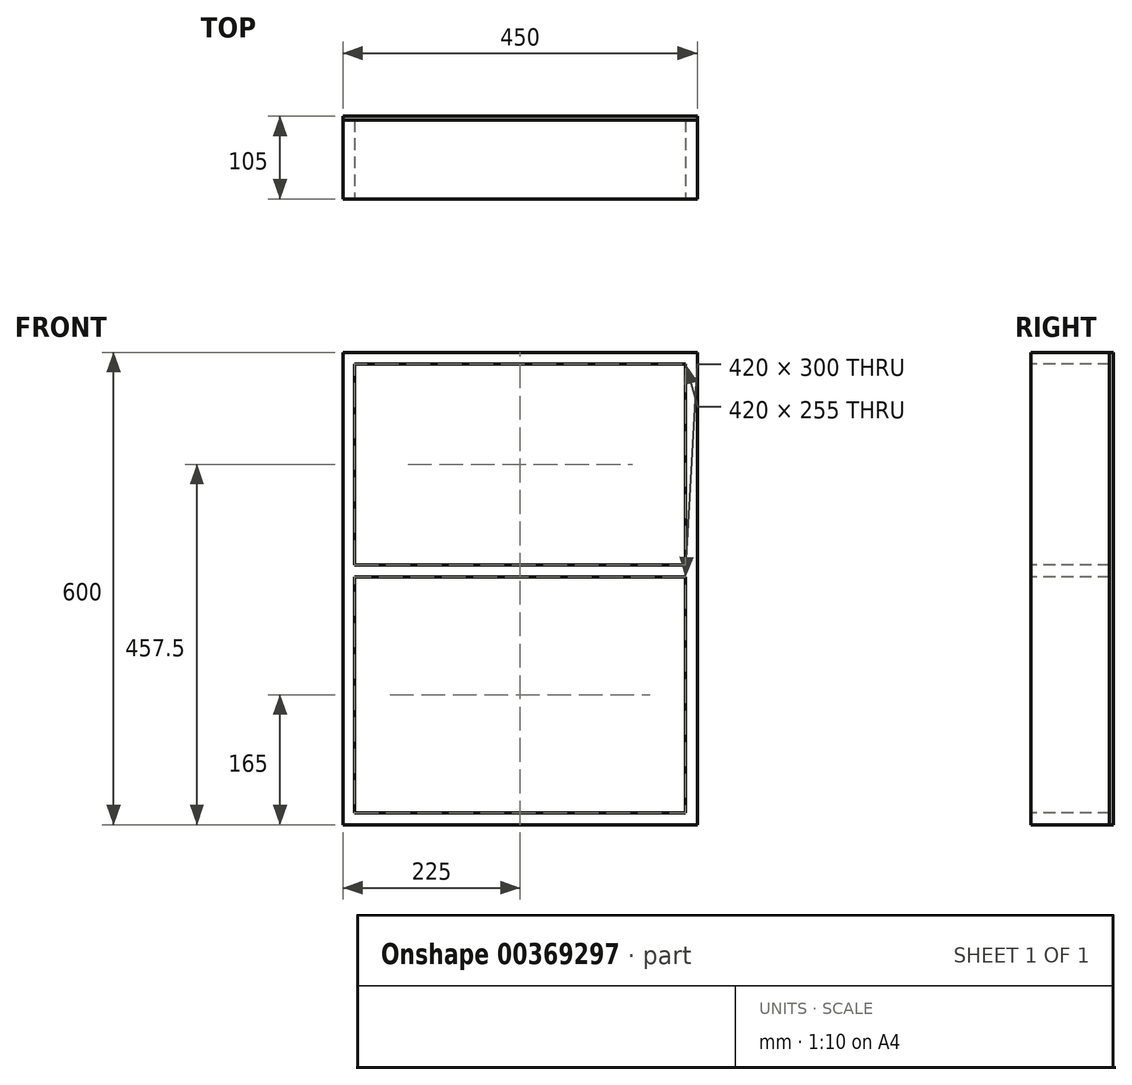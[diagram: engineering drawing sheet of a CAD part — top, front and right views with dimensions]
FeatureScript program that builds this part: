
annotation { "Feature Type Name" : "Feature", "Feature Type Description" : "" }
export const myFeature = defineFeature(function(context is Context, id is Id, definition is map)
    precondition{}
    {
        {
            var Q0;
            Q0=qCreatedBy(makeId("Top.planeOp"),FACE);
            var sketch = newSketch(context, id + "F0", { "sketchPlane" : qUnion([Q0])});
            skLineSegment(sketch, "E0.bottom", {"start": v(0, 0) * mm, "end": v(450, 0) * mm});
            skLineSegment(sketch, "E0.top", {"start": v(0, 100) * mm, "end": v(450, 100) * mm});
            skLineSegment(sketch, "E0.left", {"start": v(0, 0) * mm, "end": v(0, 100) * mm});
            skLineSegment(sketch, "E0.right", {"start": v(450, 0) * mm, "end": v(450, 100) * mm});
            skSolve(sketch);
        }
        {
            var Q0;
            Q0=makeQuery(id+"F0.imprint","IMPRINT",FACE,{"disambiguationData":[TD([[makeQuery(id+"F0.imprint","IMPRINT",EDGE,{"derivedFrom":sQuery(id+"F0.wireOp",EDGE,"E0.bottom")}),1.0]])]});
            extrude(context, id + "F1", {"entities" : qUnion([Q0]), "depth" : 15 * mm});
        }
        {
            var Q0;
            Q0=makeQuery(id+"F1.opExtrude","CAP_FACE",FACE,{"disambiguationData":[OSD([sQuery(id+"F0.wireOp",EDGE,"E0.bottom"),sQuery(id+"F0.wireOp",EDGE,"E0.top"),sQuery(id+"F0.wireOp",EDGE,"E0.left"),sQuery(id+"F0.wireOp",EDGE,"E0.right")])],"isStart":false});
            var sketch = newSketch(context, id + "F2", { "sketchPlane" : qUnion([Q0])});
            skLineSegment(sketch, "E1", {"start": v(0, 100) * mm, "end": v(15, 100) * mm});
            skLineSegment(sketch, "E2", {"start": v(0, 0) * mm, "end": v(15, 0) * mm});
            skLineSegment(sketch, "E3", {"start": v(15, 100) * mm, "end": v(15, 0) * mm});
            skLineSegment(sketch, "E4", {"start": v(450, 100) * mm, "end": v(435, 100) * mm});
            skLineSegment(sketch, "E5", {"start": v(450, 0) * mm, "end": v(435, 0) * mm});
            skLineSegment(sketch, "E6", {"start": v(435, 100) * mm, "end": v(435, 0) * mm});
            skSolve(sketch);
        }
        {
            var Q0;
            Q0=makeQuery(id+"F2.imprint","IMPRINT",FACE,{"disambiguationData":[TD([[makeQuery(id+"F2.imprint","IMPRINT",EDGE,{"derivedFrom":sQuery(id+"F2.wireOp",EDGE,"E1")}),-1.0]])]});
            var Q1;
            Q1=makeQuery(id+"F2.imprint","IMPRINT",FACE,{"disambiguationData":[TD([[makeQuery(id+"F2.imprint","IMPRINT",EDGE,{"derivedFrom":sQuery(id+"F2.wireOp",EDGE,"E4")}),-1.0]])]});
            extrude(context, id + "F3", {"entities" : qUnion([Q0, Q1]), "operationType" : NewBodyOperationType.ADD, "depth" : 570 * mm});
        }
        {
            var Q0;
            Q0=makeQuery(id+"F3.opExtrude","CAP_FACE",FACE,{"disambiguationData":[OSD([sQuery(id+"F0.wireOp",EDGE,"E0.right"),sQuery(id+"F2.wireOp",EDGE,"E4"),sQuery(id+"F2.wireOp",EDGE,"E5"),sQuery(id+"F2.wireOp",EDGE,"E6")])],"isStart":false});
            var sketch = newSketch(context, id + "F4", { "sketchPlane" : qUnion([Q0])});
            skLineSegment(sketch, "E7", {"start": v(450, 0) * mm, "end": v(0, 0) * mm});
            skLineSegment(sketch, "E8", {"start": v(450, 100) * mm, "end": v(0, 100) * mm});
            skLineSegment(sketch, "E9", {"start": v(450, 100) * mm, "end": v(450, 0) * mm});
            skLineSegment(sketch, "E10", {"start": v(0, 100) * mm, "end": v(0, 0) * mm});
            skSolve(sketch);
        }
        {
            var Q0;
            {var subQ2=sQuery(id+"F4.wireOp",EDGE,"E10");Q0=makeQuery(id+"F4.imprint","IMPRINT",FACE,{"disambiguationData":[TD([[makeQuery(id+"F4.imprint","IMPRINT",EDGE,{"derivedFrom":subQ2}),1.0]])]});}
            var Q1;
            {var subQ0=sQuery(id+"F4.wireOp",EDGE,"E9");Q1=makeQuery(id+"F4.imprint","IMPRINT",FACE,{"disambiguationData":[TD([[makeQuery(id+"F4.imprint","IMPRINT",EDGE,{"derivedFrom":subQ0}),1.0]])]});}
            extrude(context, id + "F5", {"entities" : qUnion([Q0, Q1]), "operationType" : NewBodyOperationType.ADD, "depth" : 15 * mm});
        }
        {
            var Q0;
            Q0=makeQuery(id+"F3.opExtrude","SWEPT_FACE",FACE,{"disambiguationData":[OSD([sQuery(id+"F2.wireOp",EDGE,"E3")])]});
            var sketch = newSketch(context, id + "F6", { "sketchPlane" : qUnion([Q0])});
            skLineSegment(sketch, "E11", {"start": v(100, 15) * mm, "end": v(100, 315) * mm, "construction": true});
            skLineSegment(sketch, "E12", {"start": v(100, 315) * mm, "end": v(100, 330) * mm});
            skLineSegment(sketch, "E13", {"start": v(100, 315) * mm, "end": v(0, 315) * mm});
            skLineSegment(sketch, "E14", {"start": v(100, 330) * mm, "end": v(0, 330) * mm});
            skLineSegment(sketch, "E15", {"start": v(0, 330) * mm, "end": v(0, 315) * mm});
            skSolve(sketch);
        }
        {
            var Q0;
            Q0=makeQuery(id+"F6.imprint","IMPRINT",FACE,{"disambiguationData":[TD([[makeQuery(id+"F6.imprint","IMPRINT",EDGE,{"derivedFrom":sQuery(id+"F6.wireOp",EDGE,"E12")}),-1.0]])]});
            extrude(context, id + "F7", {"entities" : qUnion([Q0]), "operationType" : NewBodyOperationType.ADD, "endBound" : BoundingType.UP_TO_NEXT, "depth" : 420 * mm});
        }
        {
            var Q0;
            Q0=makeQuery(id+"F7.boolean.opBoolean","MERGE",FACE,{"derivedFrom":[makeQuery(id+"F5.boolean.opBoolean","MERGE",FACE,{"derivedFrom":[makeQuery(id+"F3.boolean.opBoolean","MERGE",FACE,{"derivedFrom":[makeQuery(id+"F1.opExtrude","SWEPT_FACE",FACE,{"disambiguationData":[OSD([sQuery(id+"F0.wireOp",EDGE,"E0.top")])]}),makeQuery(id+"F3.opExtrude","SWEPT_FACE",FACE,{"disambiguationData":[OSD([sQuery(id+"F2.wireOp",EDGE,"E1")])]}),makeQuery(id+"F3.opExtrude","SWEPT_FACE",FACE,{"disambiguationData":[OSD([sQuery(id+"F2.wireOp",EDGE,"E4")])]})]}),makeQuery(id+"F5.opExtrude","SWEPT_FACE",FACE,{"disambiguationData":[OSD([sQuery(id+"F4.wireOp",EDGE,"E8")])]})]}),makeQuery(id+"F7.opExtrude","SWEPT_FACE",FACE,{"disambiguationData":[OSD([sQuery(id+"F6.wireOp",EDGE,"E12")])]})]});
            var sketch = newSketch(context, id + "F8", { "sketchPlane" : qUnion([Q0])});
            skLineSegment(sketch, "E16", {"start": v(0, 600) * mm, "end": v(-450, 600) * mm});
            skLineSegment(sketch, "E17", {"start": v(-450, 600) * mm, "end": v(-450, 0) * mm});
            skLineSegment(sketch, "E18", {"start": v(-450, 0) * mm, "end": v(0, 0) * mm});
            skLineSegment(sketch, "E19", {"start": v(0, 0) * mm, "end": v(0, 600) * mm});
            skSolve(sketch);
        }
        {
            var Q0;
            Q0=makeQuery(id+"F8.imprint","IMPRINT",FACE,{"disambiguationData":[TD([[makeQuery(id+"F8.imprint","IMPRINT",EDGE,{"derivedFrom":sQuery(id+"F8.wireOp",EDGE,"E16")}),-1.0]])]});
            var Q1;
            {var subQ0=sQuery(id+"F4.wireOp",EDGE,"E8");Q1=makeQuery(id+"F8.imprint","IMPRINT",FACE,{"disambiguationData":[TD([[makeQuery(id+"F8.imprint","IMPRINT",EDGE,{"derivedFrom":makeQuery(id+"F5.opExtrude","CAP_EDGE",EDGE,{"disambiguationData":[OSD([subQ0])],"isStart":true})}),-1.0]])]});}
            var Q2;
            {var subQ0=sQuery(id+"F0.wireOp",EDGE,"E0.top");Q2=makeQuery(id+"F8.imprint","IMPRINT",FACE,{"disambiguationData":[TD([[makeQuery(id+"F8.imprint","IMPRINT",EDGE,{"derivedFrom":makeQuery(id+"F1.opExtrude","CAP_EDGE",EDGE,{"disambiguationData":[OSD([subQ0])],"isStart":false})}),-1.0]])]});}
            extrude(context, id + "F9", {"entities" : qUnion([Q0, Q1, Q2]), "depth" : 5 * mm});
        }
    });
